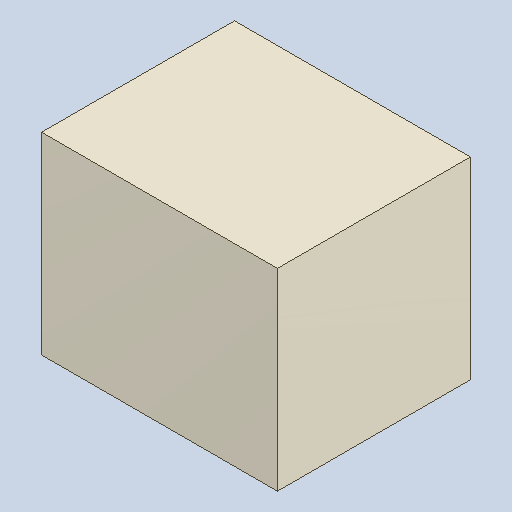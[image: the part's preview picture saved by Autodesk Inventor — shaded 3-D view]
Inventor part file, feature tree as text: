
AUTODESK INVENTOR PART (.ipt)
format: ipt  version: 2023.4 (Build 274418000, 418)  size: 81,920 bytes
history: native  units: mm
features: extrude x1
ambient origin geometry x8: Origin, YZ Plane, XZ Plane, XY Plane, X Axis, Y Axis, Z Axis, Center Point
bodies: Solid1 (feature_tree)
feature tree (1):
  extrude  "Extruded_14"  [1 undecoded]
note: 1 required parameter value undecoded (feature->parameter linkage not recoverable at this tier; creation-order binding heuristic only, values carry confidence <= 0.55)
